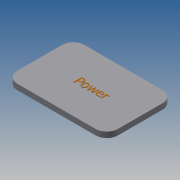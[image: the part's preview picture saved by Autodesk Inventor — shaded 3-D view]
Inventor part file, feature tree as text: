
AUTODESK INVENTOR PART (.ipt)
format: ipt  version: 2014 SP1 (Build 180222100, 222)  size: 213,504 bytes
history: native  units: in
note: dims shown in document units (in); Inventor stores cm internally (conversion verified against a paired STEP export)
features: sketch x2, extrude x1, emboss x1
ambient origin geometry x8: Origin, YZ Plane, XZ Plane, XY Plane, X Axis, Y Axis, Z Axis, Center Point
bodies: Solid1 (feature_tree)
feature tree (4):
  extrude  "Extrusion1"  Depth=24.0in
  emboss  "Emboss1"
  sketch  "Sketch1"  dims[d0=36.0in d1=24.0in]
  sketch  "Sketch8"  dims[d2=2.0in d3=0.0in d9=4.0in d53=0.1in d54=0.0in]
